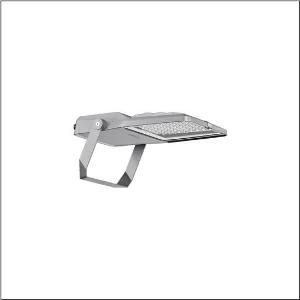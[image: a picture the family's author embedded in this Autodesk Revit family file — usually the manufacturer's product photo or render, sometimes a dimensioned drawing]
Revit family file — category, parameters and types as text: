
# Revit family: floodlight_fl_21_iq_mini___pl52_5xa7771d4d1a_c00e
name_source: partatom
category: Lighting Fixtures
units: mm (PartAtom-declared; Revit-internal decimal feet)

## family parameters
Cut with Voids When Loaded = No
Host = Face
Light Source = No
Part Type = Normal
Room Calculation Point = No
Round Connector Dimension = Use Diameter
Shared = No

## types (1)
- --- (1 x LED, 18610 lm, 143 W, 4000K)
    Apparent Load = 143 VA
    CIE Flux Codes = 26 60 98 100 100
    Color Rendering = 70
    Color Temperature = 4000K
    Default Elevation = 1800 mm
    Description = Floodlight FL 21 iQ mini, floodlight, primary light control with lens, of PMMA, primary optical cover: protective disc, of toughened safety glass, transparent, light distribution: PL52, light emission: direct distribution, installation type: surface-mounted, LED, High Power LED, rated luminous flux: 18.610lm, luminous efficacy: 130lm/W, light colour: 740, colour temperature: 4000K, control: Auto-Match, Temp-Guard, Lumen-Switch, Night-Set, Smart-Wire, Light-Fading, Desk-Remote (wireless, voltage-free reading and setting of iQ features in the workshop via application-optimized NFC function/RFID function), optimised constant luminous flux control (CLO 2.0), with terminal, 6-pole, mains connection: 220..240V, AC, 50/60Hz, start of lifetime: 143W, end of service life: 152W, reduction: 61W, luminaire housing, of diecast aluminium, powder-coated, Siteco® metallic grey (DB 702S), corrosivity category C5 mid according to DIN EN ISO 12944, sealing non-destructively replaceable, mounting bracket, of steel, galvanised, powder-coated, Siteco® metallic grey (DB 702S), protection rating (complete): IP66, insulation class (complete): insulation class II (safety insulation), certification: CE, ENEC, VDE, protection symbol: D, impact resistance: IK08, permissible operating ambient temperature: -40..+40°C, permissible operating ambient temperature for outdoor applications: -40..+50°C, standard: DIN EN 12944, LABS conformity tested according to VDMA 24364:2018-05, packaging unit: 1 piece

Light Distribution: PL52
    Height = 70 mm
    Lamp = 1 x LED
    Lamp Light Flux = 18610 lm
    Lamp Power = 143 W
    Lamp count = 1
    Length = 485 mm
    Luminous efficacy = 130 lm/W
    Manufacturer = Siteco
    ModVariant = No
    Model = 5XA7771D4D1A
    Number of Poles = 1
    OnlyDefault = Yes
    Power Factor = 1
    Product Name = Floodlight FL 21 iQ mini | PL52
    Product group = floodlight | pylon annexe
    ProductGroupID = 6200
    Protection Class = Protection class II
    Protection Degree = IP 66
    RLX_Detail_Level = 1
    RLX_Emergency_Light_Flux = 0 lm
    RLX_Emergency_Type = 0
    RLX_Emergency_Type_DB = No
    RlxData = <blob elided: 96605 chars, md5=9d52c0dc>
    Socket = socket
    Standby Power = 0 W
    System Light Flux = 18610 lm
    System Power = 143 W
    Type Comments = factory setting: luminous flux: 100 % | dim-lin: 254 | 730 mA
    Type Image = l_1006845.jpg
    URL = http://relux.com
    VarID = @adj_096239
    Voltage = 0 V
    Weight = 0.00 kg
    Width = 337 mm

## geometry (parser evidence)
native form markers: Blend x4, Sweep x10
no freeform markers — native parametric forms only
